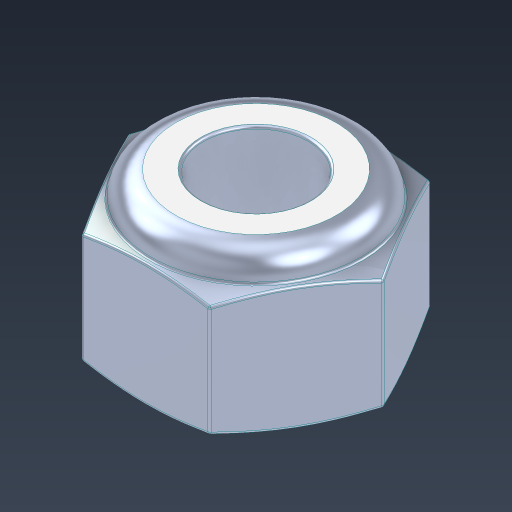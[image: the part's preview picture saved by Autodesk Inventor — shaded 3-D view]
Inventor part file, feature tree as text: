
AUTODESK INVENTOR PART (.ipt)
format: ipt  version: 2024.3 (Build 283343000, 343)  size: 248,832 bytes
history: native  units: in
note: dims shown in document units (in); Inventor stores cm internally (conversion verified against a paired STEP export)
features: fillet x1
ambient origin geometry x8: Origin, YZ Plane, XZ Plane, XY Plane, X Axis, Y Axis, Z Axis, Center Point
bodies: Solid1 (feature_tree)
feature tree (1):
  fillet  "Fillet2"  [1 undecoded]
note: 1 required parameter value undecoded (feature->parameter linkage not recoverable at this tier; creation-order binding heuristic only, values carry confidence <= 0.55)
